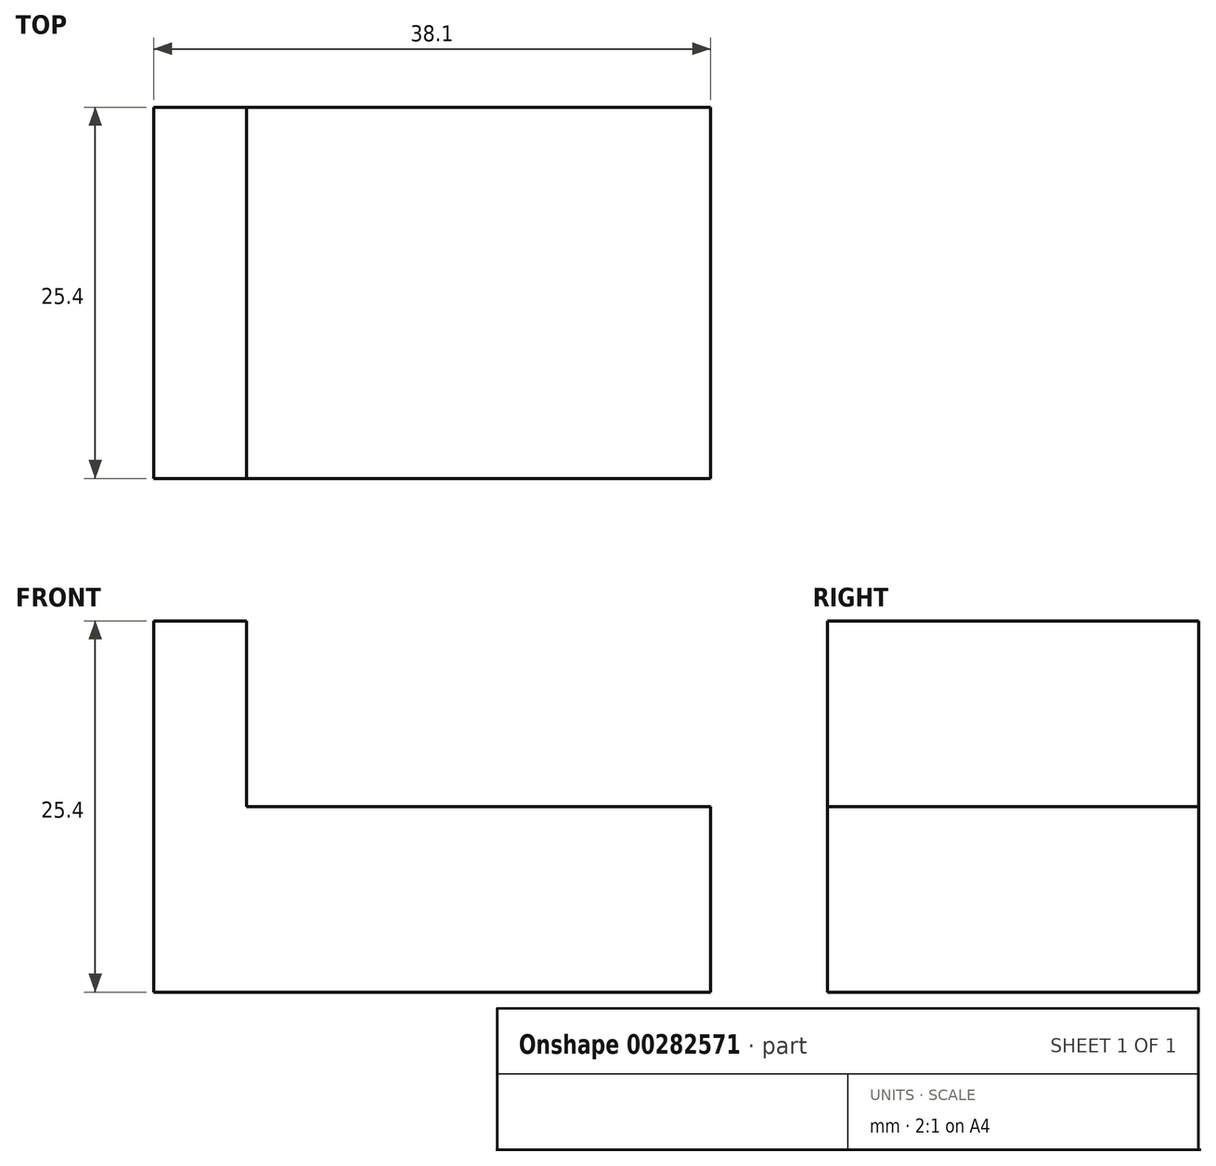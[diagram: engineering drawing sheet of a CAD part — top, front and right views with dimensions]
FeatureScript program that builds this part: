
annotation { "Feature Type Name" : "Feature", "Feature Type Description" : "" }
export const myFeature = defineFeature(function(context is Context, id is Id, definition is map)
    precondition{}
    {
        {
            var Q0;
            Q0=qCreatedBy(makeId("Front.planeOp"),FACE);
            var sketch = newSketch(context, id + "F0", { "sketchPlane" : qUnion([Q0])});
            skLineSegment(sketch, "E0", {"start": v(0, 0) * mm, "end": v(-38.1, 0) * mm});
            skLineSegment(sketch, "E1", {"start": v(-38.1, 0) * mm, "end": v(-38.1, 25.4) * mm});
            skLineSegment(sketch, "E2", {"start": v(-38.1, 25.4) * mm, "end": v(-31.75, 25.4) * mm});
            skLineSegment(sketch, "E3", {"start": v(-31.75, 25.4) * mm, "end": v(-31.75, 12.7) * mm});
            skLineSegment(sketch, "E4", {"start": v(-31.75, 12.7) * mm, "end": v(0, 12.7) * mm});
            skLineSegment(sketch, "E5", {"start": v(0, 12.7) * mm, "end": v(0, 0) * mm});
            skSolve(sketch);
        }
        {
            var Q0;
            Q0=makeQuery(id+"F0.imprint","IMPRINT",FACE,{"disambiguationData":[TD([[makeQuery(id+"F0.imprint","IMPRINT",EDGE,{"derivedFrom":sQuery(id+"F0.wireOp",EDGE,"E0")}),-1.0]])]});
            extrude(context, id + "F1", {"entities" : qUnion([Q0]), "oppositeDirection" : true, "depth" : 25.4 * mm});
        }
    });
